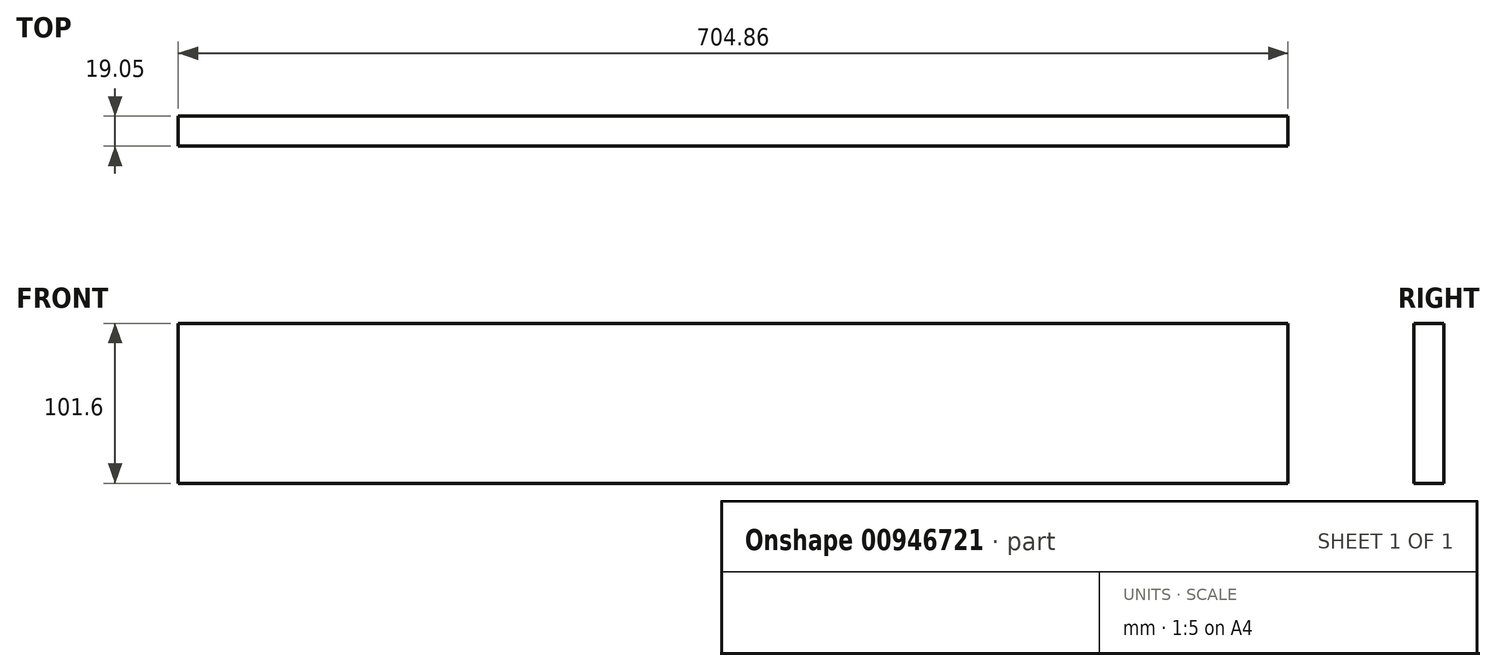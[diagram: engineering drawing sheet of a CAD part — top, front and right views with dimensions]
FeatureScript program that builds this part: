
annotation { "Feature Type Name" : "Feature", "Feature Type Description" : "" }
export const myFeature = defineFeature(function(context is Context, id is Id, definition is map)
    precondition{}
    {
        {
            var Q0;
            Q0=qCreatedBy(makeId("Front.planeOp"),FACE);
            var sketch = newSketch(context, id + "F0", { "sketchPlane" : qUnion([Q0])});
            skLineSegment(sketch, "E0.bottom", {"start": v(-352.43, 50.8) * mm, "end": v(352.43, 50.8) * mm});
            skLineSegment(sketch, "E0.top", {"start": v(-352.43, -50.8) * mm, "end": v(352.43, -50.8) * mm});
            skLineSegment(sketch, "E0.left", {"start": v(-352.43, 50.8) * mm, "end": v(-352.43, -50.8) * mm});
            skLineSegment(sketch, "E0.right", {"start": v(352.43, 50.8) * mm, "end": v(352.43, -50.8) * mm});
            skPoint(sketch, "E0.middle", {"position": v(0, 0) * mm});
            skSolve(sketch);
        }
        {
            var Q0;
            Q0=makeQuery(id+"F0.imprint","IMPRINT",FACE,{"disambiguationData":[TD([[makeQuery(id+"F0.imprint","IMPRINT",EDGE,{"derivedFrom":sQuery(id+"F0.wireOp",EDGE,"E0.bottom")}),-1.0]])]});
            extrude(context, id + "F1", {"entities" : qUnion([Q0]), "depth" : 19.05 * mm, "offsetDistance" : 25.4 * mm});
        }
    });
